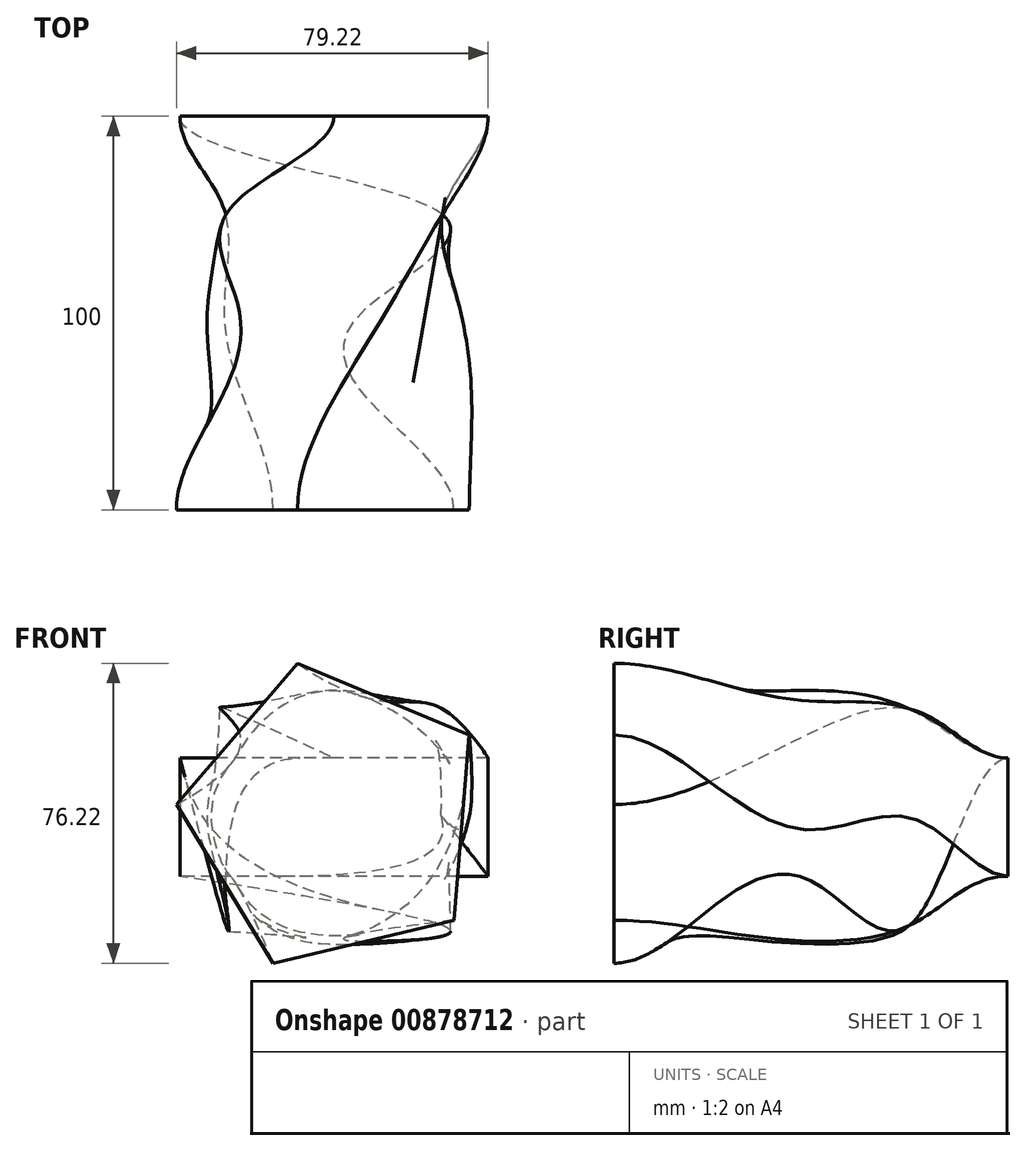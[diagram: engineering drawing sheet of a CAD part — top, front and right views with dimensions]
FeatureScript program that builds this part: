
annotation { "Feature Type Name" : "Feature", "Feature Type Description" : "" }
export const myFeature = defineFeature(function(context is Context, id is Id, definition is map)
    precondition{}
    {
        {
            var Q0;
            Q0=qCreatedBy(makeId("Front.planeOp"),FACE);
            cPlane(context, id + "F0", {"entities" : qUnion([Q0]), "cplaneType" : CPlaneType.OFFSET, "offset" : 25 * mm, "width" : 150 * mm, "height" : 150 * mm});
        }
        {
            var Q0;
            Q0=qCreatedBy(id+"F0.planeOp",FACE);
            cPlane(context, id + "F1", {"entities" : qUnion([Q0]), "cplaneType" : CPlaneType.OFFSET, "offset" : 25 * mm, "width" : 150 * mm, "height" : 150 * mm});
        }
        {
            var Q0;
            Q0=qCreatedBy(id+"F1.planeOp",FACE);
            cPlane(context, id + "F2", {"entities" : qUnion([Q0]), "cplaneType" : CPlaneType.OFFSET, "offset" : 25 * mm, "width" : 150 * mm, "height" : 150 * mm});
        }
        {
            var Q0;
            Q0=qCreatedBy(id+"F2.planeOp",FACE);
            cPlane(context, id + "F3", {"entities" : qUnion([Q0]), "cplaneType" : CPlaneType.OFFSET, "offset" : 25 * mm, "width" : 150 * mm, "height" : 150 * mm});
        }
        {
            var Q0;
            Q0=qCreatedBy(makeId("Front.planeOp"),FACE);
            var sketch = newSketch(context, id + "F4", { "sketchPlane" : qUnion([Q0])});
            skLineSegment(sketch, "E0.bottom", {"start": v(39.15, 15.02) * mm, "end": v(-39.15, 15.02) * mm});
            skLineSegment(sketch, "E0.top", {"start": v(39.15, -15.02) * mm, "end": v(-39.15, -15.02) * mm});
            skLineSegment(sketch, "E0.left", {"start": v(39.15, 15.02) * mm, "end": v(39.15, -15.02) * mm});
            skLineSegment(sketch, "E0.right", {"start": v(-39.15, 15.02) * mm, "end": v(-39.15, -15.02) * mm});
            skPoint(sketch, "E0.middle", {"position": v(0, 0) * mm});
            skSolve(sketch);
        }
        {
            var Q0;
            Q0=qCreatedBy(id+"F0.planeOp",FACE);
            var sketch = newSketch(context, id + "F5", { "sketchPlane" : qUnion([Q0])});
            skLineSegment(sketch, "E1.bottom", {"start": v(27.5, 27.5) * mm, "end": v(-27.5, 27.5) * mm});
            skLineSegment(sketch, "E1.top", {"start": v(27.5, -27.5) * mm, "end": v(-27.5, -27.5) * mm});
            skLineSegment(sketch, "E1.left", {"start": v(27.5, 27.5) * mm, "end": v(27.5, -27.5) * mm});
            skLineSegment(sketch, "E1.right", {"start": v(-27.5, 27.5) * mm, "end": v(-27.5, -27.5) * mm});
            skPoint(sketch, "E1.middle", {"position": v(0, 0) * mm});
            skSolve(sketch);
        }
        {
            var Q0;
            Q0=qCreatedBy(id+"F1.planeOp",FACE);
            var sketch = newSketch(context, id + "F6", { "sketchPlane" : qUnion([Q0])});
            skCircle(sketch, "E2", {"center": v(0, 0) * mm, "radius": 32.22 * mm});
            skPoint(sketch, "E3", {"position": v(-27.84, -16.21) * mm});
            skSolve(sketch);
        }
        {
            var Q0;
            Q0=qCreatedBy(id+"F3.planeOp",FACE);
            var sketch = newSketch(context, id + "F7", { "sketchPlane" : qUnion([Q0])});
            skCircle(sketch, "E4.cCircle", {"center": v(0, 0) * mm, "radius": 40.2 * mm, "construction": true});
            skLineSegment(sketch, "E4.0", {"start": v(34.33, 20.93) * mm, "end": v(30.5, -26.18) * mm});
            skLineSegment(sketch, "E4.1", {"start": v(30.5, -26.18) * mm, "end": v(-15.47, -37.1) * mm});
            skLineSegment(sketch, "E4.2", {"start": v(-15.47, -37.1) * mm, "end": v(-40.07, 3.25) * mm});
            skLineSegment(sketch, "E4.3", {"start": v(-40.07, 3.25) * mm, "end": v(-9.3, 39.11) * mm});
            skLineSegment(sketch, "E4.4", {"start": v(-9.3, 39.11) * mm, "end": v(34.33, 20.93) * mm});
            skSolve(sketch);
        }
        {
            var Q0;
            Q0=makeQuery(id+"F7.imprint","IMPRINT",FACE,{"disambiguationData":[TD([[makeQuery(id+"F7.imprint","IMPRINT",EDGE,{"derivedFrom":sQuery(id+"F7.wireOp",EDGE,"E4.0")}),-1.0]])]});
            var Q1;
            Q1=makeQuery(id+"F6.imprint","IMPRINT",FACE,{"disambiguationData":[TD([[makeQuery(id+"F6.imprint","IMPRINT",EDGE,{"derivedFrom":sQuery(id+"F6.wireOp",EDGE,"E2")}),1.0]])]});
            var Q2;
            Q2=makeQuery(id+"F5.imprint","IMPRINT",FACE,{"disambiguationData":[TD([[makeQuery(id+"F5.imprint","IMPRINT",EDGE,{"derivedFrom":sQuery(id+"F5.wireOp",EDGE,"E1.bottom")}),1.0]])]});
            var Q3;
            Q3=makeQuery(id+"F4.imprint","IMPRINT",FACE,{"disambiguationData":[TD([[makeQuery(id+"F4.imprint","IMPRINT",EDGE,{"derivedFrom":sQuery(id+"F4.wireOp",EDGE,"E0.bottom")}),1.0]])]});
            var Q4;
            Q4=sQuery(id+"F4.wireOp",VERTEX,"E0.bottom.end");
            var Q5;
            Q5=sQuery(id+"F5.wireOp",VERTEX,"E1.top.end");
            var Q6;
            Q6=sQuery(id+"F6.wireOp",VERTEX,"E3");
            var Q7;
            Q7=sQuery(id+"F7.wireOp",VERTEX,"E4.1.end");
            loft(context, id + "F8", {"startCondition" : LoftEndDerivativeType.NORMAL_TO_PROFILE, "startMagnitude" : 1, "endCondition" : LoftEndDerivativeType.NORMAL_TO_PROFILE, "endMagnitude" : 1, "sheetProfilesArray" : [{ "sheetProfileEntities" : qUnion([Q0]) }, { "sheetProfileEntities" : qUnion([Q1]) }, { "sheetProfileEntities" : qUnion([Q2]) }, { "sheetProfileEntities" : qUnion([Q3]) }], "matchConnections" : true, "connections" : [{ "connectionEntities" : qUnion([Q4, Q5, Q6, Q7]), "connectionEdgeQueries" : qUnion([]), "connectionEdgeParameters" : [] }]});
        }
    });
